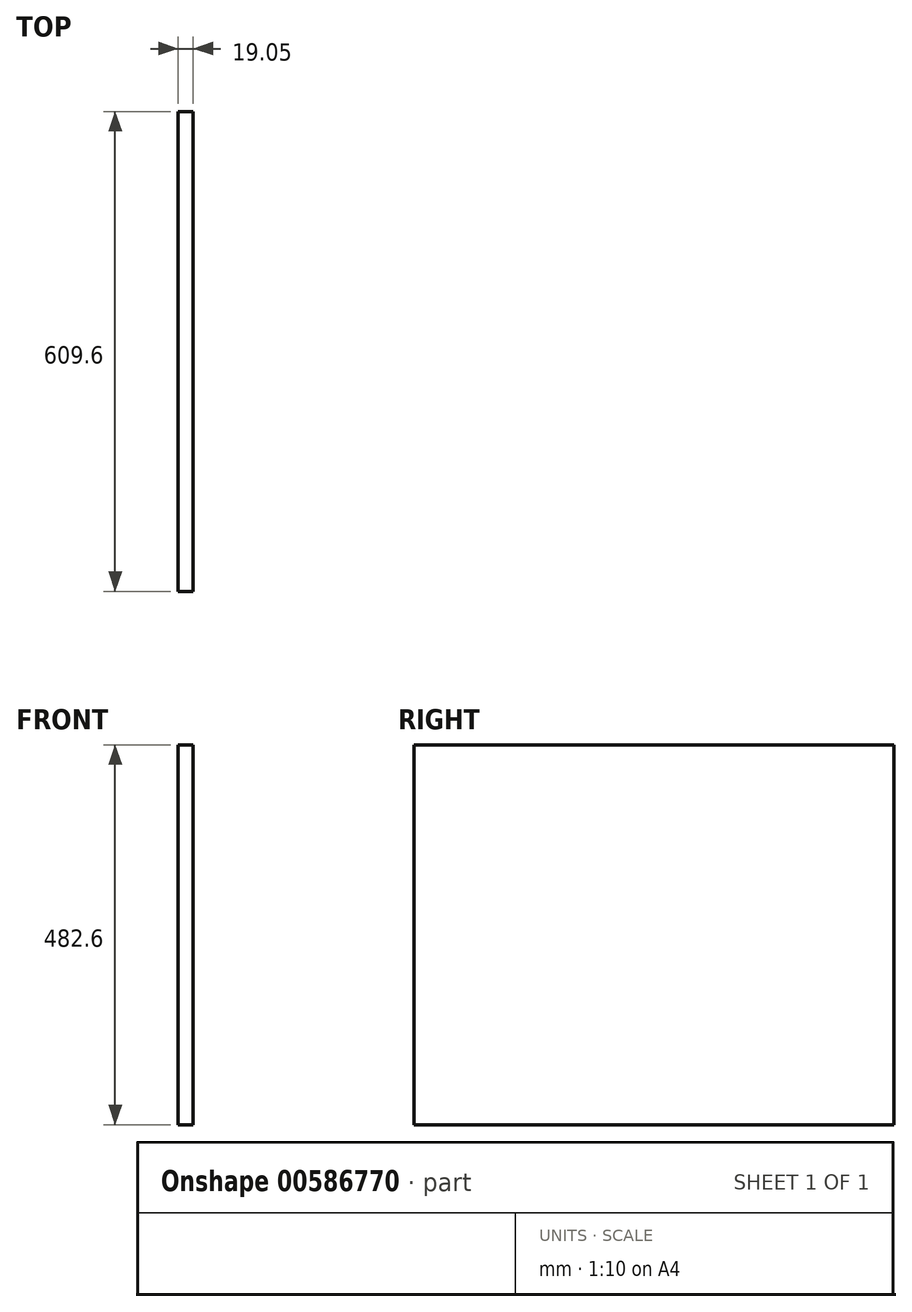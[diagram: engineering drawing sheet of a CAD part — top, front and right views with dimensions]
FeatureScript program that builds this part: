
annotation { "Feature Type Name" : "Feature", "Feature Type Description" : "" }
export const myFeature = defineFeature(function(context is Context, id is Id, definition is map)
    precondition{}
    {
        {
            var Q0;
            Q0=qCreatedBy(makeId("Right.planeOp"),FACE);
            var sketch = newSketch(context, id + "F0", { "sketchPlane" : qUnion([Q0])});
            skLineSegment(sketch, "E0.bottom", {"start": v(-31.57, 448.97) * mm, "end": v(578.03, 448.97) * mm});
            skLineSegment(sketch, "E0.top", {"start": v(-31.57, -33.63) * mm, "end": v(578.03, -33.63) * mm});
            skLineSegment(sketch, "E0.left", {"start": v(-31.57, 448.97) * mm, "end": v(-31.57, -33.63) * mm});
            skLineSegment(sketch, "E0.right", {"start": v(578.03, 448.97) * mm, "end": v(578.03, -33.63) * mm});
            skSolve(sketch);
        }
        {
            var Q0;
            Q0 = qSketchRegion(id + "F0", true);
            extrude(context, id + "F1", {"entities" : qUnion([Q0]), "depth" : 19.05 * mm, "offsetDistance" : 25.4 * mm});
        }
    });
